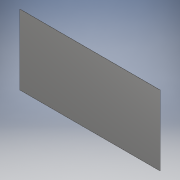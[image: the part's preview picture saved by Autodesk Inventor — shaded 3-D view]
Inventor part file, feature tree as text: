
AUTODESK INVENTOR PART (.ipt)
format: ipt  version: 2019 (Build 230136000, 136)  size: 90,624 bytes
history: native  units: in
note: dims shown in document units (in); Inventor stores cm internally (conversion verified against a paired STEP export)
features: other x1, extrude x1, sketch x1
ambient origin geometry x8: Origin, YZ Plane, XZ Plane, XY Plane, X Axis, Y Axis, Z Axis, Center Point
bodies: Body1 (feature_tree)
feature tree (3):
  other  "Galvanized steel sheet"
  extrude  "Extrusion1"  Depth=60.0in
  sketch  "Sketch1"  dims[d0=120.0in d1=60.0in d2=0.108in d3=0.0in]
